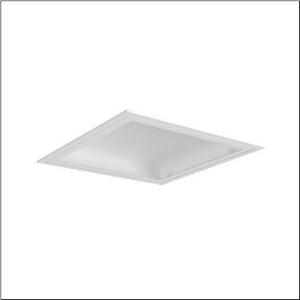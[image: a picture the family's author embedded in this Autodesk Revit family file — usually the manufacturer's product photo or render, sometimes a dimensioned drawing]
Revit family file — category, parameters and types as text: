
# Revit family: mira_r__21_51fr427a472a_c216
name_source: partatom
category: Lighting Fixtures
units: mm (PartAtom-declared; Revit-internal decimal feet)

## family parameters
Cut with Voids When Loaded = No
Host = Face
Light Source = No
Part Type = Normal
Room Calculation Point = No
Round Connector Dimension = Use Diameter
Shared = No

## types (1)
- Mira® 21 (1 x LED, 7680 lm, 66 W, 4000K)
    Apparent Load = 66 VA
    CIE Flux Codes = 50 81 97 100 100
    Color Rendering = 80
    Color Temperature = 4000K
    Default Elevation = 1800 mm
    Description = Mira® 21, clean room luminaire, primary light control with reflector, primary optical cover: cover, of PC, light emission: direct distribution, primary light characteristic: symmetric, installation type: recessed, LED, rated luminous flux: 7.680lm, luminous efficacy: 116lm/W, light colour: 840, colour temperature: 4000K, control gear: ECG, with terminal, 3-pole, max. 2.5mm², mains connection: 230V, AC, 50/60Hz, rated input power: 66W, luminaire housing, of sheet steel, coated, pure white, module: M625, length: 623mm, width: 623mm, height: 115mm, protection rating (complete): IP54, insulation class (complete): insulation class I (protective earthing), certification: CE, UKCA, permissible operating ambient temperature: -5..+40°C, standard: EN 50419, packaging unit: 1 piece
    Height = 0 mm  [stored 0 ft]
    Lamp = 1 x LED
    Lamp Light Flux = 7680 lm
    Lamp Power = 66 W
    Lamp count = 1
    Length = 625 mm
    Luminous efficacy = 116 lm/W
    Manufacturer = Siteco
    ModVariant = No
    Model = 51FR427A472A
    Mounting Place = Ceiling
    Mounting Type = Recessed
    Number of Poles = 1
    OnlyDefault = Yes
    Power Factor = 1
    Product Name = Mira® 21
    Product group = clean room luminaire
    ProductGroupID = 401
    Protection Class = Protection class I
    Protection Degree = IP 54
    RLX_Detail_Level = 1
    RlxData = <blob elided: 13309 chars, md5=bbdf7f05>
    Socket = socket
    Standby Power = 0 W
    System Light Flux = 7680 lm
    System Power = 66 W
    Type Comments = Product without accessories
    Type Image = l_1007109.jpg
    URL = http://relux.com
    VarID = ---
    Voltage = 0 V
    Weight = 0.00 kg
    Width = 625 mm

note: [stored X ft] marks values corroborated as IEEE doubles in the binary element streams (Revit-internal decimal feet)

## geometry (parser evidence)
native form markers: Sweep x8
no freeform markers — native parametric forms only
